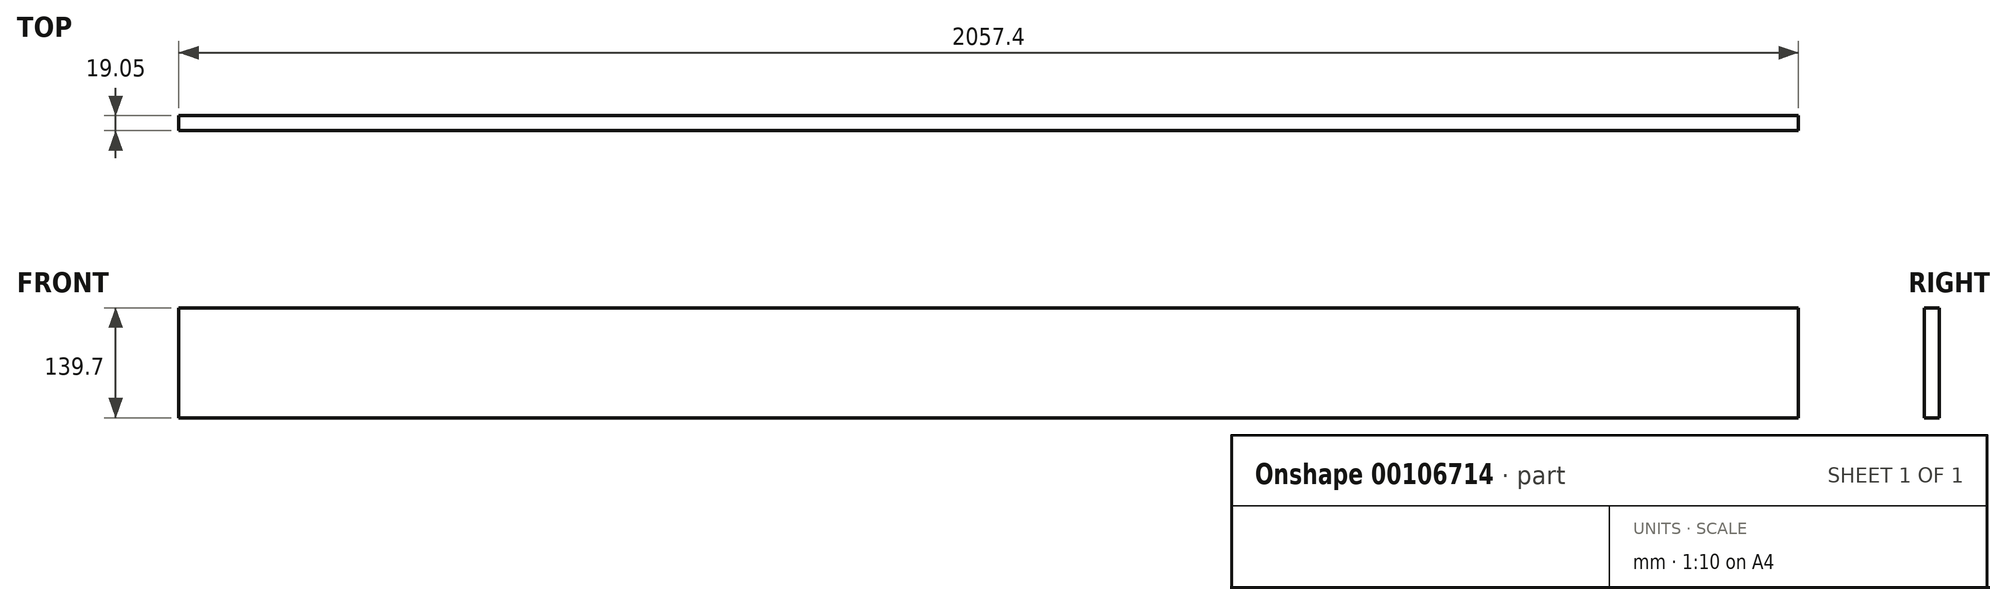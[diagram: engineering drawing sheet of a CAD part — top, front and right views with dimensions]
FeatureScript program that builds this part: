
annotation { "Feature Type Name" : "Feature", "Feature Type Description" : "" }
export const myFeature = defineFeature(function(context is Context, id is Id, definition is map)
    precondition{}
    {
        {
            var Q0;
            Q0=qCreatedBy(makeId("Front.planeOp"),FACE);
            var sketch = newSketch(context, id + "F0", { "sketchPlane" : qUnion([Q0])});
            skLineSegment(sketch, "E0.bottom", {"start": v(0, 0) * mm, "end": v(2057.4, 0) * mm});
            skLineSegment(sketch, "E0.top", {"start": v(0, 139.7) * mm, "end": v(2057.4, 139.7) * mm});
            skLineSegment(sketch, "E0.left", {"start": v(0, 0) * mm, "end": v(0, 139.7) * mm});
            skLineSegment(sketch, "E0.right", {"start": v(2057.4, 0) * mm, "end": v(2057.4, 139.7) * mm});
            skSolve(sketch);
        }
        {
            var Q0;
            Q0=makeQuery(id+"F0.imprint","IMPRINT",FACE,{"disambiguationData":[TD([[makeQuery(id+"F0.imprint","IMPRINT",EDGE,{"derivedFrom":sQuery(id+"F0.wireOp",EDGE,"E0.bottom")}),1.0]])]});
            extrude(context, id + "F1", {"entities" : qUnion([Q0]), "depth" : 19.05 * mm});
        }
    });
